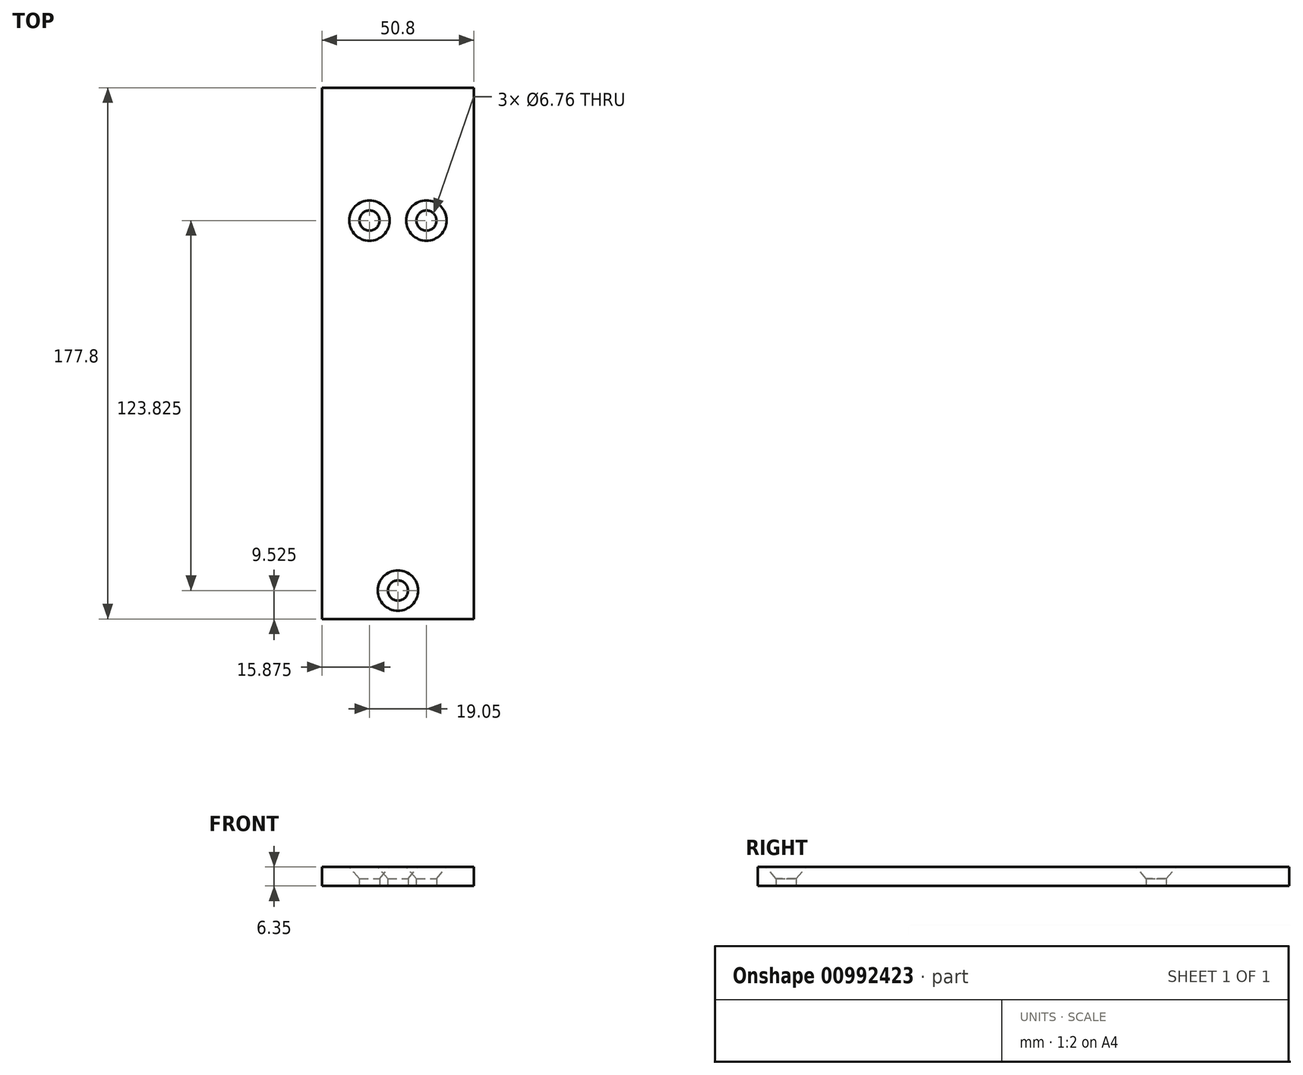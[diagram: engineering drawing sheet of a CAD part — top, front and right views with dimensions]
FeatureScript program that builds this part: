
annotation { "Feature Type Name" : "Feature", "Feature Type Description" : "" }
export const myFeature = defineFeature(function(context is Context, id is Id, definition is map)
    precondition{}
    {
        {
            var Q0;
            Q0=qCreatedBy(makeId("Top.planeOp"),FACE);
            var sketch = newSketch(context, id + "F0", { "sketchPlane" : qUnion([Q0])});
            skLineSegment(sketch, "E0.bottom", {"start": v(25.4, 88.9) * mm, "end": v(-25.4, 88.9) * mm});
            skLineSegment(sketch, "E0.top", {"start": v(25.4, -88.9) * mm, "end": v(-25.4, -88.9) * mm});
            skLineSegment(sketch, "E0.left", {"start": v(25.4, 88.9) * mm, "end": v(25.4, -88.9) * mm});
            skLineSegment(sketch, "E0.right", {"start": v(-25.4, 88.9) * mm, "end": v(-25.4, -88.9) * mm});
            skPoint(sketch, "E0.middle", {"position": v(0, 0) * mm});
            skCircle(sketch, "E1", {"center": v(0, -79.38) * mm, "radius": 3.57 * mm});
            skCircle(sketch, "E2", {"center": v(-9.52, 44.45) * mm, "radius": 3.57 * mm});
            skCircle(sketch, "E3", {"center": v(9.52, 44.45) * mm, "radius": 3.57 * mm});
            skSolve(sketch);
        }
        {
            var Q0;
            Q0=makeQuery(id+"F0.imprint","IMPRINT",FACE,{"disambiguationData":[TD([[makeQuery(id+"F0.imprint","IMPRINT",EDGE,{"derivedFrom":sQuery(id+"F0.wireOp",EDGE,"E0.bottom")}),1.0]])]});
            var Q1;
            Q1=makeQuery(id+"F0.imprint","IMPRINT",FACE,{"disambiguationData":[TD([[makeQuery(id+"F0.imprint","IMPRINT",EDGE,{"derivedFrom":sQuery(id+"F0.wireOp",EDGE,"E2")}),1.0]])]});
            var Q2;
            Q2=makeQuery(id+"F0.imprint","IMPRINT",FACE,{"disambiguationData":[TD([[makeQuery(id+"F0.imprint","IMPRINT",EDGE,{"derivedFrom":sQuery(id+"F0.wireOp",EDGE,"E3")}),1.0]])]});
            var Q3;
            Q3=makeQuery(id+"F0.imprint","IMPRINT",FACE,{"disambiguationData":[TD([[makeQuery(id+"F0.imprint","IMPRINT",EDGE,{"derivedFrom":sQuery(id+"F0.wireOp",EDGE,"E1")}),1.0]])]});
            extrude(context, id + "F1", {"entities" : qUnion([Q0, Q1, Q2, Q3]), "oppositeDirection" : true, "depth" : 6.35 * mm, "offsetDistance" : 25.4 * mm});
        }
        {
            var Q0;
            Q0=sQuery(id+"F0.wireOp",VERTEX,"E2.center");
            var Q1;
            Q1=sQuery(id+"F0.wireOp",VERTEX,"E3.center");
            var Q2;
            Q2=sQuery(id+"F0.wireOp",VERTEX,"E1.center");
            var Q3;
            Q3=makeQuery(id+"F1.opExtrude","SWEPT_BODY",BODY,{"disambiguationData":[OSD([sQuery(id+"F0.wireOp",EDGE,"E0.bottom"),sQuery(id+"F0.wireOp",EDGE,"E0.top"),sQuery(id+"F0.wireOp",EDGE,"E0.left"),sQuery(id+"F0.wireOp",EDGE,"E0.right")])]});
            hole(context, id + "F2", {"style" : HoleStyle.C_SINK, "endStyle" : HoleEndStyle.THROUGH, "standardTappedOrClearance" : lookupTablePath({ "fit" : "Close (ASME)", "standard" : "ANSI", "size" : "1/4", "type" : "Clearance" }), "standardBlindInLast" : lookupTablePath({ "fit" : "Close", "standard" : "ANSI", "engagement" : "75%", "pitch" : "20 tpi", "size" : "1/4", "type" : "Clearance & tapped" }), "holeDiameter" : 6.76 * mm, "cSinkDiameter" : 13.5 * mm, "cSinkAngle" : 82 * degree, "majorDiameter" : 6.35 * mm, "isTappedThrough" : true, "tappedDepth" : 12.7 * mm, "tapClearance" : 3, "locations" : qUnion([Q0, Q1, Q2]), "scope" : qUnion([Q3]), "startStyle" : HoleStartStyle.SKETCH});
        }
    });
